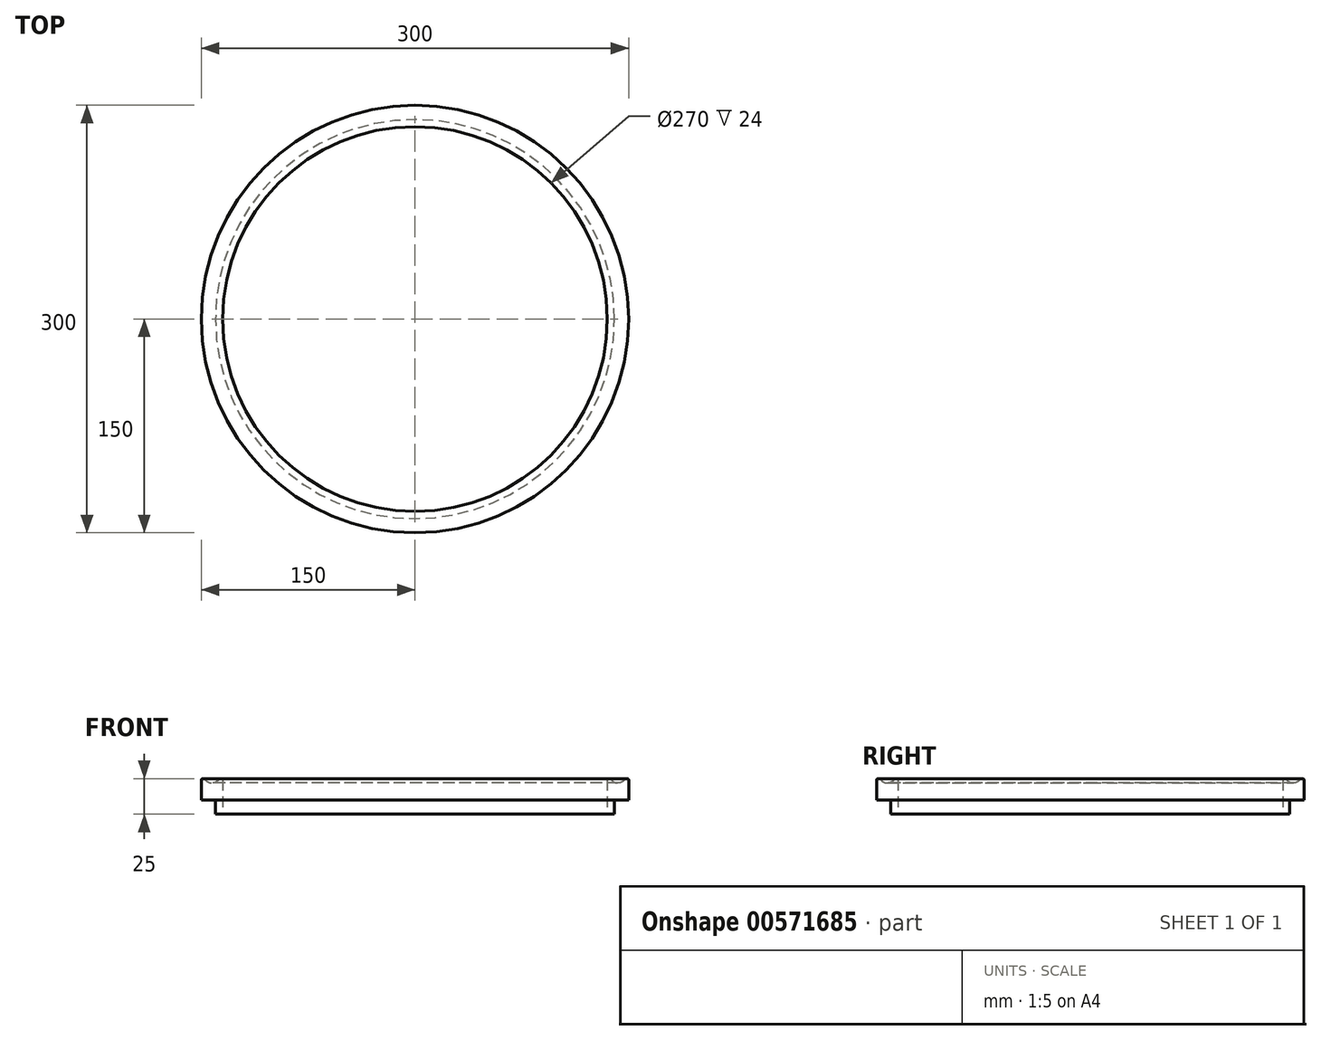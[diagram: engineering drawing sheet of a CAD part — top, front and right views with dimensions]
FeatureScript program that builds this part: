
annotation { "Feature Type Name" : "Feature", "Feature Type Description" : "" }
export const myFeature = defineFeature(function(context is Context, id is Id, definition is map)
    precondition{}
    {
        {
            var Q0;
            Q0=qCreatedBy(makeId("Top.planeOp"),FACE);
            var sketch = newSketch(context, id + "F0", { "sketchPlane" : qUnion([Q0])});
            skCircle(sketch, "E0", {"center": v(0, 0) * mm, "radius": 150 * mm});
            skCircle(sketch, "E1", {"center": v(0, 0) * mm, "radius": 135 * mm});
            skSolve(sketch);
        }
        {
            var Q0;
            Q0=makeQuery(id+"F0.imprint","IMPRINT",FACE,{"disambiguationData":[TD([[makeQuery(id+"F0.imprint","IMPRINT",EDGE,{"derivedFrom":sQuery(id+"F0.wireOp",EDGE,"E0")}),1.0]])]});
            extrude(context, id + "F1", {"entities" : qUnion([Q0]), "depth" : 25 * mm, "offsetDistance" : 25 * mm});
        }
        {
            var Q0;
            Q0=makeQuery(id+"F1.opExtrude","CAP_FACE",FACE,{"disambiguationData":[OSD([sQuery(id+"F0.wireOp",EDGE,"E0"),sQuery(id+"F0.wireOp",EDGE,"E1")])],"isStart":true});
            var sketch = newSketch(context, id + "F2", { "sketchPlane" : qUnion([Q0])});
            skCircle(sketch, "E2", {"center": v(0, 0) * mm, "radius": 150 * mm});
            skCircle(sketch, "E3", {"center": v(0, 0) * mm, "radius": 140 * mm});
            skSolve(sketch);
        }
        {
            var Q0;
            Q0 = qSketchRegion(id + "F2", true);
            extrude(context, id + "F3", {"entities" : qUnion([Q0]), "operationType" : NewBodyOperationType.REMOVE, "oppositeDirection" : true, "depth" : 10 * mm, "offsetDistance" : 25 * mm});
        }
        {
            var Q0;
            Q0=makeQuery(id+"F1.opExtrude","CAP_FACE",FACE,{"disambiguationData":[OSD([sQuery(id+"F0.wireOp",EDGE,"E0"),sQuery(id+"F0.wireOp",EDGE,"E1")])],"isStart":false});
            var sketch = newSketch(context, id + "F4", { "sketchPlane" : qUnion([Q0])});
            skCircle(sketch, "E4", {"center": v(0, 0) * mm, "radius": 137.5 * mm});
            skCircle(sketch, "E5", {"center": v(0, 0) * mm, "radius": 147.5 * mm});
            skSolve(sketch);
        }
        {
            var Q0;
            Q0 = qSketchRegion(id + "F4", true);
            extrude(context, id + "F5", {"entities" : qUnion([Q0]), "operationType" : NewBodyOperationType.REMOVE, "oppositeDirection" : true, "depth" : 3 * mm, "offsetDistance" : 25 * mm});
        }
        {
            var Q0;
            Q0=makeQuery(id+"F5.boolean.opBoolean","COPY",EDGE,{"derivedFrom":makeQuery(id+"F5.opExtrude","CAP_EDGE",EDGE,{"disambiguationData":[OSD([sQuery(id+"F4.wireOp",EDGE,"E4")])],"isStart":false})});
            var Q1;
            Q1=makeQuery(id+"F5.boolean.opBoolean","COPY",EDGE,{"derivedFrom":makeQuery(id+"F5.opExtrude","CAP_EDGE",EDGE,{"disambiguationData":[OSD([sQuery(id+"F4.wireOp",EDGE,"E5")])],"isStart":false})});
            fillet(context, id + "F6", {"entities" : qUnion([Q0, Q1]), "radius" : 5 * mm, "tangentPropagation" : true, "allowEdgeOverflow" : false});
        }
        {
            var Q0;
            {var subQ0=sQuery(id+"F0.wireOp",EDGE,"E0");var subQ1=sQuery(id+"F4.wireOp",EDGE,"E5");Q0=makeQuery(id+"F6.opFillet","BLEND_EDGE",EDGE,{"blendedFrom":[makeQuery(id+"F5.boolean.opBoolean","COPY",EDGE,{"derivedFrom":makeQuery(id+"F5.opExtrude","CAP_EDGE",EDGE,{"disambiguationData":[OSD([subQ1])],"isStart":false})}),makeQuery(id+"F5.boolean.opBoolean","SPLIT",FACE,{"disambiguationData":[TD([makeQuery(id+"F1.opExtrude","SWEPT_FACE",FACE,{"disambiguationData":[OSD([subQ0])]})])],"derivedFrom":makeQuery(id+"F1.opExtrude","CAP_FACE",FACE,{"disambiguationData":[OSD([subQ0,sQuery(id+"F0.wireOp",EDGE,"E1")])],"isStart":false})})],"blendedInto":[makeQuery(id+"F5.boolean.opBoolean","SPLIT",FACE,{"disambiguationData":[TD([makeQuery(id+"F1.opExtrude","SWEPT_FACE",FACE,{"disambiguationData":[OSD([subQ0])]})])],"derivedFrom":makeQuery(id+"F1.opExtrude","CAP_FACE",FACE,{"disambiguationData":[OSD([subQ0,sQuery(id+"F0.wireOp",EDGE,"E1")])],"isStart":false})})]});}
            var Q1;
            Q1=makeQuery(id+"F1.opExtrude","CAP_EDGE",EDGE,{"disambiguationData":[OSD([sQuery(id+"F0.wireOp",EDGE,"E0")])],"isStart":false});
            fillet(context, id + "F7", {"entities" : qUnion([Q0, Q1]), "radius" : 1 * mm, "tangentPropagation" : true, "allowEdgeOverflow" : false});
        }
        {
            var Q0;
            {var subQ0=sQuery(id+"F0.wireOp",EDGE,"E1");var subQ1=sQuery(id+"F4.wireOp",EDGE,"E4");Q0=makeQuery(id+"F6.opFillet","BLEND_EDGE",EDGE,{"blendedFrom":[makeQuery(id+"F5.boolean.opBoolean","COPY",EDGE,{"derivedFrom":makeQuery(id+"F5.opExtrude","CAP_EDGE",EDGE,{"disambiguationData":[OSD([subQ1])],"isStart":false})}),makeQuery(id+"F5.boolean.opBoolean","SPLIT",FACE,{"disambiguationData":[TD([makeQuery(id+"F1.opExtrude","SWEPT_FACE",FACE,{"disambiguationData":[OSD([subQ0])]})])],"derivedFrom":makeQuery(id+"F1.opExtrude","CAP_FACE",FACE,{"disambiguationData":[OSD([sQuery(id+"F0.wireOp",EDGE,"E0"),subQ0])],"isStart":false})})],"blendedInto":[makeQuery(id+"F5.boolean.opBoolean","SPLIT",FACE,{"disambiguationData":[TD([makeQuery(id+"F1.opExtrude","SWEPT_FACE",FACE,{"disambiguationData":[OSD([subQ0])]})])],"derivedFrom":makeQuery(id+"F1.opExtrude","CAP_FACE",FACE,{"disambiguationData":[OSD([sQuery(id+"F0.wireOp",EDGE,"E0"),subQ0])],"isStart":false})})]});}
            var Q1;
            Q1=makeQuery(id+"F1.opExtrude","CAP_EDGE",EDGE,{"disambiguationData":[OSD([sQuery(id+"F0.wireOp",EDGE,"E1")])],"isStart":false});
            fillet(context, id + "F8", {"entities" : qUnion([Q0, Q1]), "radius" : 1 * mm, "tangentPropagation" : true, "allowEdgeOverflow" : false});
        }
    });
